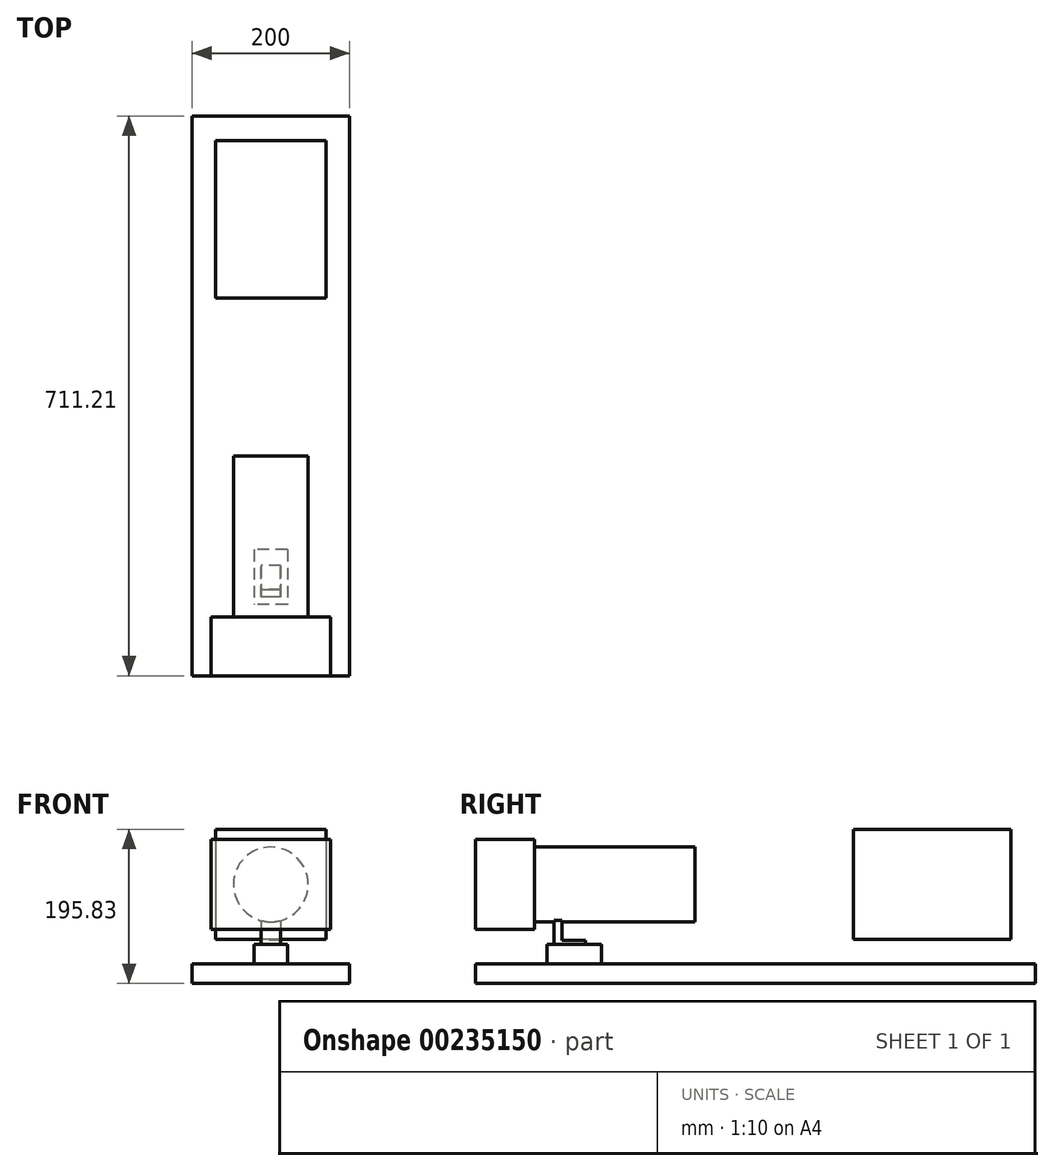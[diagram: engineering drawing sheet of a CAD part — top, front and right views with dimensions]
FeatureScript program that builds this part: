
annotation { "Feature Type Name" : "Feature", "Feature Type Description" : "" }
export const myFeature = defineFeature(function(context is Context, id is Id, definition is map)
    precondition{}
    {
        {
            var Q0;
            Q0=qCreatedBy(makeId("Top.planeOp"),FACE);
            var sketch = newSketch(context, id + "F0", { "sketchPlane" : qUnion([Q0])});
            skLineSegment(sketch, "E0.bottom", {"start": v(-100, 0) * mm, "end": v(100, 0) * mm});
            skLineSegment(sketch, "E0.top", {"start": v(-100, 711.2) * mm, "end": v(100, 711.2) * mm});
            skLineSegment(sketch, "E0.left", {"start": v(-100, 0) * mm, "end": v(-100, 711.2) * mm});
            skLineSegment(sketch, "E0.right", {"start": v(100, 0) * mm, "end": v(100, 711.2) * mm});
            skSolve(sketch);
        }
        {
            var Q0;
            Q0 = qSketchRegion(id + "F0", true);
            extrude(context, id + "F1", {"entities" : qUnion([Q0]), "oppositeDirection" : true, "depth" : 25 * mm});
        }
        {
            var Q0;
            Q0=qCreatedBy(makeId("Right.planeOp"),FACE);
            var sketch = newSketch(context, id + "F2", { "sketchPlane" : qUnion([Q0])});
            skLineSegment(sketch, "E1", {"start": v(100, 25) * mm, "end": v(140, 25) * mm});
            skLineSegment(sketch, "E2", {"start": v(140, 25) * mm, "end": v(140, 30) * mm});
            skLineSegment(sketch, "E3", {"start": v(140, 30) * mm, "end": v(110, 30) * mm});
            skLineSegment(sketch, "E4", {"start": v(110, 30) * mm, "end": v(110, 55) * mm});
            skLineSegment(sketch, "E5", {"start": v(110, 55) * mm, "end": v(100, 55) * mm});
            skLineSegment(sketch, "E6", {"start": v(100, 55) * mm, "end": v(100, 25) * mm});
            skSolve(sketch);
        }
        {
            var Q0;
            Q0 = qSketchRegion(id + "F2", true);
            extrude(context, id + "F3", {"entities" : qUnion([Q0]), "endBound" : BoundingType.SYMMETRIC, "depth" : 25 * mm});
        }
        {
            var Q0;
            Q0=qCreatedBy(makeId("Front.planeOp"),FACE);
            cPlane(context, id + "F4", {"entities" : qUnion([Q0]), "cplaneType" : CPlaneType.OFFSET, "offset" : 100 * mm, "oppositeDirection" : true, "width" : 150 * mm, "height" : 150 * mm});
        }
        {
            var Q0;
            Q0=qCreatedBy(id+"F4.planeOp",FACE);
            var sketch = newSketch(context, id + "F5", { "sketchPlane" : qUnion([Q0])});
            skCircle(sketch, "E7", {"center": v(0, 100.83) * mm, "radius": 47.5 * mm});
            skSolve(sketch);
        }
        {
            var Q0;
            Q0 = qSketchRegion(id + "F5", true);
            extrude(context, id + "F6", {"entities" : qUnion([Q0]), "operationType" : NewBodyOperationType.ADD, "oppositeDirection" : true, "depth" : (204 - 25) * mm, "hasSecondDirection" : true, "secondDirectionOppositeDirection" : false, "secondDirectionDepth" : 25 * mm});
        }
        {
            var Q0;
            Q0=makeQuery(id+"F6.opExtrude","CAP_FACE",FACE,{"disambiguationData":[OSD([sQuery(id+"F5.wireOp",EDGE,"E7")])],"isStart":true});
            var sketch = newSketch(context, id + "F7", { "sketchPlane" : qUnion([Q0])});
            skLineSegment(sketch, "E8.bottom", {"start": v(76, 43.83) * mm, "end": v(-76, 43.83) * mm});
            skLineSegment(sketch, "E8.top", {"start": v(76, 157.83) * mm, "end": v(-76, 157.83) * mm});
            skLineSegment(sketch, "E8.left", {"start": v(76, 43.83) * mm, "end": v(76, 157.83) * mm});
            skLineSegment(sketch, "E8.right", {"start": v(-76, 43.83) * mm, "end": v(-76, 157.83) * mm});
            skPoint(sketch, "E8.middle", {"position": v(0, 100.83) * mm});
            skSolve(sketch);
        }
        {
            var Q0;
            Q0 = qSketchRegion(id + "F7", true);
            extrude(context, id + "F8", {"entities" : qUnion([Q0]), "depth" : 75 * mm});
        }
        {
            var Q0;
            Q0=makeQuery(id+"F1.opExtrude","CAP_FACE",FACE,{"disambiguationData":[OSD([sQuery(id+"F0.wireOp",EDGE,"E0.bottom"),sQuery(id+"F0.wireOp",EDGE,"E0.top"),sQuery(id+"F0.wireOp",EDGE,"E0.left"),sQuery(id+"F0.wireOp",EDGE,"E0.right")])],"isStart":true});
            var sketch = newSketch(context, id + "F9", { "sketchPlane" : qUnion([Q0])});
            skLineSegment(sketch, "E9.bottom", {"start": v(21.04, 160.34) * mm, "end": v(-21.04, 160.34) * mm});
            skLineSegment(sketch, "E9.top", {"start": v(21.04, 90.63) * mm, "end": v(-21.04, 90.63) * mm});
            skLineSegment(sketch, "E9.left", {"start": v(21.04, 160.34) * mm, "end": v(21.04, 90.63) * mm});
            skLineSegment(sketch, "E9.right", {"start": v(-21.04, 160.34) * mm, "end": v(-21.04, 90.63) * mm});
            skPoint(sketch, "E9.middle", {"position": v(0, 125.48) * mm});
            skSolve(sketch);
        }
        {
            var Q0;
            Q0 = qSketchRegion(id + "F9", true);
            var Q1;
            Q1=makeQuery(id+"F3.opExtrude","SWEPT_FACE",FACE,{"disambiguationData":[OSD([sQuery(id+"F2.wireOp",EDGE,"E1")])]});
            var Q2;
            Q2=makeQuery(id+"F3.opExtrude","SWEPT_BODY",BODY,{"disambiguationData":[OSD([sQuery(id+"F2.wireOp",EDGE,"E1"),sQuery(id+"F2.wireOp",EDGE,"E2"),sQuery(id+"F2.wireOp",EDGE,"E3"),sQuery(id+"F2.wireOp",EDGE,"E4"),sQuery(id+"F2.wireOp",EDGE,"E5"),sQuery(id+"F2.wireOp",EDGE,"E6")])]});
            extrude(context, id + "F10", {"entities" : qUnion([Q0]), "endBound" : BoundingType.UP_TO_SURFACE, "endBoundEntityFace" : qUnion([Q1]), "endBoundEntityBody" : qUnion([Q2]), "depth" : 25 * mm});
        }
        {
            var Q0;
            Q0=makeQuery(id+"F8.opExtrude","SWEPT_FACE",FACE,{"disambiguationData":[OSD([sQuery(id+"F7.wireOp",EDGE,"E8.top")])]});
            var Q1;
            Q1=makeQuery(id+"F8.opExtrude","SWEPT_FACE",FACE,{"disambiguationData":[OSD([sQuery(id+"F7.wireOp",EDGE,"E8.bottom")])]});
            cPlane(context, id + "F11", {"entities" : qUnion([Q0, Q1]), "cplaneType" : CPlaneType.MID_PLANE, "offset" : 25 * mm, "width" : 150 * mm, "height" : 150 * mm});
        }
        {
            var Q0;
            Q0=qCreatedBy(id+"F11.planeOp",FACE);
            var sketch = newSketch(context, id + "F12", { "sketchPlane" : qUnion([Q0])});
            skLineSegment(sketch, "E10.bottom", {"start": v(70, 680) * mm, "end": v(-70, 680) * mm});
            skLineSegment(sketch, "E10.top", {"start": v(70, 480) * mm, "end": v(-70, 480) * mm});
            skLineSegment(sketch, "E10.left", {"start": v(70, 680) * mm, "end": v(70, 480) * mm});
            skLineSegment(sketch, "E10.right", {"start": v(-70, 680) * mm, "end": v(-70, 480) * mm});
            skPoint(sketch, "E10.middle", {"position": v(0, 580) * mm});
            skSolve(sketch);
        }
        {
            var Q0;
            Q0 = qSketchRegion(id + "F12", true);
            extrude(context, id + "F13", {"entities" : qUnion([Q0]), "endBound" : BoundingType.SYMMETRIC, "depth" : 140 * mm});
        }
    });
